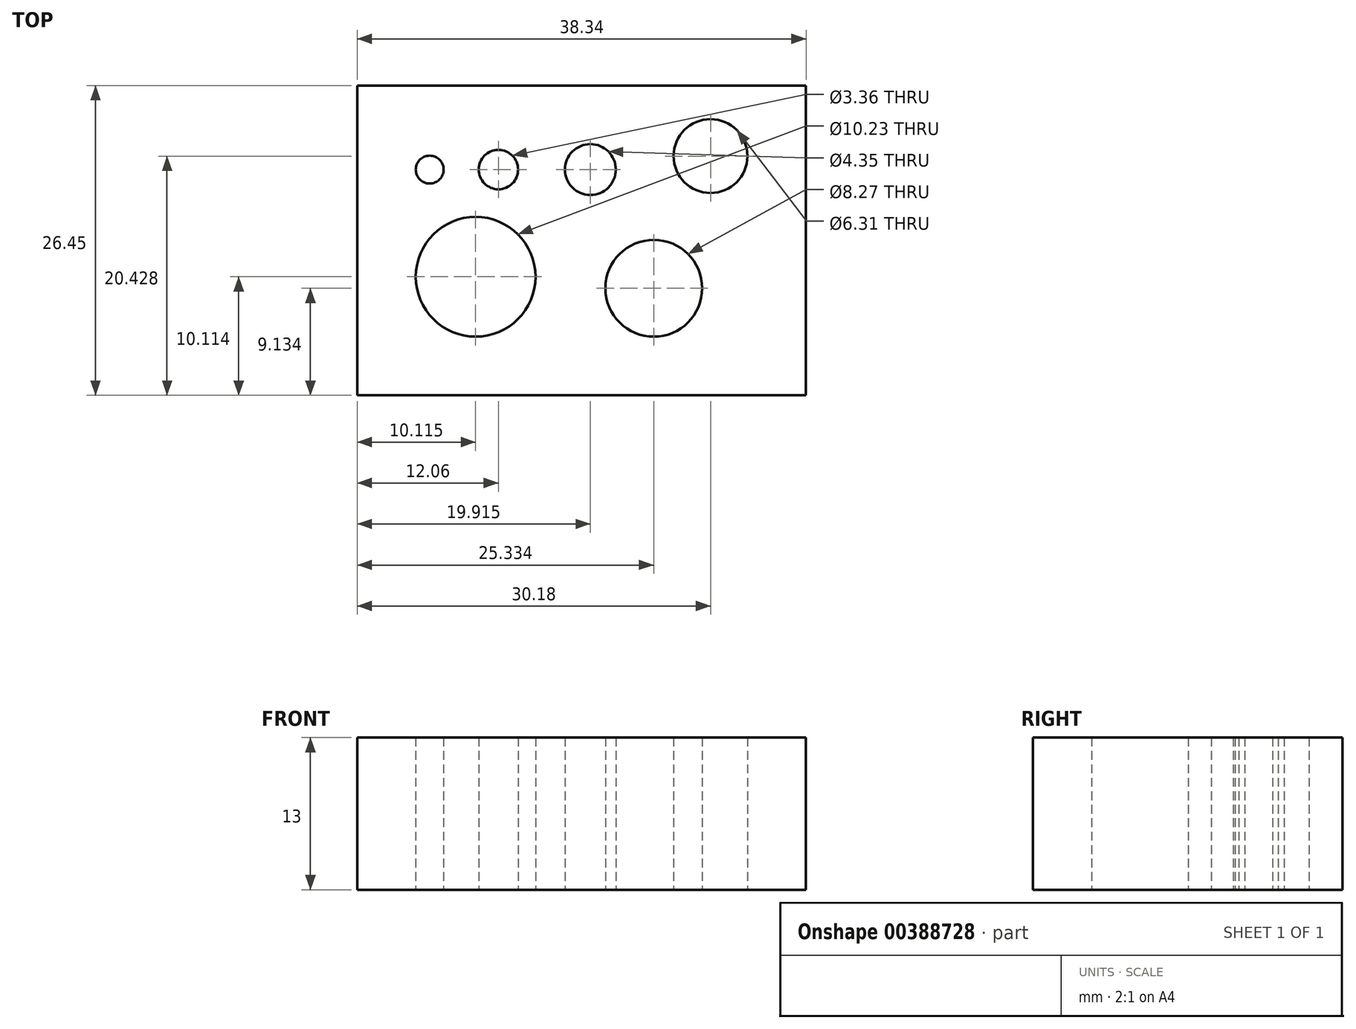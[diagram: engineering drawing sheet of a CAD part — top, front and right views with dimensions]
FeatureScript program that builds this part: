
annotation { "Feature Type Name" : "Feature", "Feature Type Description" : "" }
export const myFeature = defineFeature(function(context is Context, id is Id, definition is map)
    precondition{}
    {
        {
            var Q0;
            Q0=qCreatedBy(makeId("Top.planeOp"),FACE);
            var sketch = newSketch(context, id + "F0", { "sketchPlane" : qUnion([Q0])});
            skLineSegment(sketch, "E0.bottom", {"start": v(-14.2, 9.75) * mm, "end": v(24.15, 9.75) * mm});
            skLineSegment(sketch, "E0.top", {"start": v(-14.2, -16.7) * mm, "end": v(24.15, -16.7) * mm});
            skLineSegment(sketch, "E0.left", {"start": v(-14.2, 9.75) * mm, "end": v(-14.2, -16.7) * mm});
            skLineSegment(sketch, "E0.right", {"start": v(24.15, 9.75) * mm, "end": v(24.15, -16.7) * mm});
            skPoint(sketch, "E0.middle", {"position": v(0, 0) * mm});
            skCircle(sketch, "E1", {"center": v(-8, 2.57) * mm, "radius": 1.19 * mm});
            skCircle(sketch, "E2", {"center": v(-2.13, 2.57) * mm, "radius": 1.68 * mm});
            skCircle(sketch, "E3", {"center": v(-4.07, -6.59) * mm, "radius": 5.12 * mm});
            skCircle(sketch, "E4", {"center": v(5.73, 2.57) * mm, "radius": 2.17 * mm});
            skCircle(sketch, "E5", {"center": v(11.14, -7.57) * mm, "radius": 4.13 * mm});
            skPoint(sketch, "E6", {"position": v(-8, 0) * mm});
            skCircle(sketch, "E7", {"center": v(16, 3.73) * mm, "radius": 3.15 * mm});
            skSolve(sketch);
        }
        {
            var Q0;
            Q0=makeQuery(id+"F0.imprint","IMPRINT",FACE,{"disambiguationData":[TD([[makeQuery(id+"F0.imprint","IMPRINT",EDGE,{"derivedFrom":sQuery(id+"F0.wireOp",EDGE,"E0.bottom")}),-1.0]])]});
            extrude(context, id + "F1", {"entities" : qUnion([Q0]), "depth" : 13 * mm});
        }
    });
